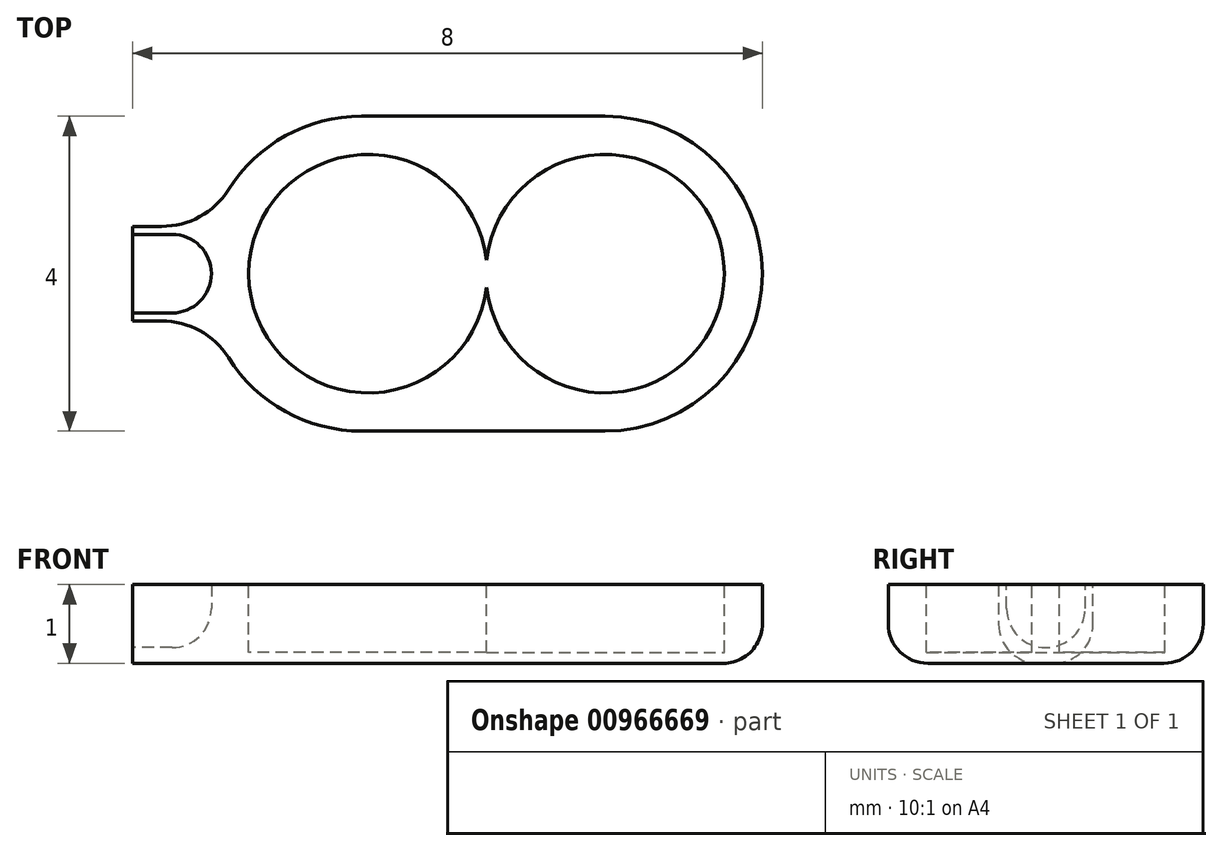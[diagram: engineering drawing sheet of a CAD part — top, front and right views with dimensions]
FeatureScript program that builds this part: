
annotation { "Feature Type Name" : "Feature", "Feature Type Description" : "" }
export const myFeature = defineFeature(function(context is Context, id is Id, definition is map)
    precondition{}
    {
        {
            var Q0;
            Q0=qCreatedBy(makeId("Top.planeOp"),FACE);
            var sketch = newSketch(context, id + "F0", { "sketchPlane" : qUnion([Q0])});
            skLineSegment(sketch, "E0.bottom", {"start": v(0, 0) * mm, "end": v(7, 0) * mm});
            skLineSegment(sketch, "E0.top", {"start": v(0, 4) * mm, "end": v(7, 4) * mm});
            skLineSegment(sketch, "E0.left", {"start": v(0, 0) * mm, "end": v(0, 4) * mm});
            skLineSegment(sketch, "E0.right", {"start": v(7, 0) * mm, "end": v(7, 4) * mm});
            skLineSegment(sketch, "E1", {"start": v(0, 2) * mm, "end": v(0, 2.6) * mm});
            skLineSegment(sketch, "E2", {"start": v(0, 2.6) * mm, "end": v(-1, 2.6) * mm});
            skLineSegment(sketch, "E3", {"start": v(-1, 2.6) * mm, "end": v(-1, 1.4) * mm});
            skLineSegment(sketch, "E4", {"start": v(-1, 1.4) * mm, "end": v(0, 1.4) * mm});
            skSolve(sketch);
        }
        {
            var Q0;
            Q0 = qSketchRegion(id + "F0", true);
            extrude(context, id + "F1", {"entities" : qUnion([Q0]), "depth" : 1 * mm, "offsetDistance" : 25 * mm});
        }
        {
            var Q0;
            Q0=makeQuery(id+"F1.opExtrude","CAP_FACE",FACE,{"disambiguationData":[OSD([sQuery(id+"F0.wireOp",EDGE,"E0.bottom"),sQuery(id+"F0.wireOp",EDGE,"E0.top"),sQuery(id+"F0.wireOp",EDGE,"E0.left"),sQuery(id+"F0.wireOp",EDGE,"E0.right"),sQuery(id+"F0.wireOp",EDGE,"E2"),sQuery(id+"F0.wireOp",EDGE,"E3"),sQuery(id+"F0.wireOp",EDGE,"E4")])],"isStart":false});
            var sketch = newSketch(context, id + "F2", { "sketchPlane" : qUnion([Q0])});
            skLineSegment(sketch, "E5", {"start": v(7, 2) * mm, "end": v(5, 2) * mm});
            skCircle(sketch, "E6", {"center": v(5, 2) * mm, "radius": 1.51 * mm});
            skSolve(sketch);
        }
        {
            var Q0;
            Q0 = qSketchRegion(id + "F2", true);
            extrude(context, id + "F3", {"entities" : qUnion([Q0]), "operationType" : NewBodyOperationType.REMOVE, "oppositeDirection" : true, "depth" : 0.86 * mm, "offsetDistance" : 25 * mm});
        }
        {
            var Q0;
            Q0=makeQuery(id+"F1.opExtrude","CAP_FACE",FACE,{"disambiguationData":[OSD([sQuery(id+"F0.wireOp",EDGE,"E0.bottom"),sQuery(id+"F0.wireOp",EDGE,"E0.top"),sQuery(id+"F0.wireOp",EDGE,"E0.left"),sQuery(id+"F0.wireOp",EDGE,"E0.right"),sQuery(id+"F0.wireOp",EDGE,"E2"),sQuery(id+"F0.wireOp",EDGE,"E3"),sQuery(id+"F0.wireOp",EDGE,"E4")])],"isStart":false});
            var sketch = newSketch(context, id + "F4", { "sketchPlane" : qUnion([Q0])});
            skLineSegment(sketch, "E7", {"start": v(7, 2) * mm, "end": v(2, 2) * mm});
            skCircle(sketch, "E8", {"center": v(2, 2) * mm, "radius": 1.51 * mm});
            skSolve(sketch);
        }
        {
            var Q0;
            Q0 = qSketchRegion(id + "F4", true);
            extrude(context, id + "F5", {"entities" : qUnion([Q0]), "operationType" : NewBodyOperationType.REMOVE, "oppositeDirection" : true, "depth" : 0.86 * mm, "offsetDistance" : 25 * mm});
        }
        {
            var Q0;
            Q0 = qSketchRegion(id + "F4", true);
            extrude(context, id + "F6", {"entities" : qUnion([Q0]), "operationType" : NewBodyOperationType.REMOVE, "oppositeDirection" : true, "depth" : 0.6 * mm, "offsetDistance" : 25 * mm});
        }
        {
            var Q0;
            Q0=makeQuery(id+"F1.opExtrude","CAP_FACE",FACE,{"disambiguationData":[OSD([sQuery(id+"F0.wireOp",EDGE,"E0.bottom"),sQuery(id+"F0.wireOp",EDGE,"E0.top"),sQuery(id+"F0.wireOp",EDGE,"E0.left"),sQuery(id+"F0.wireOp",EDGE,"E0.right"),sQuery(id+"F0.wireOp",EDGE,"E2"),sQuery(id+"F0.wireOp",EDGE,"E3"),sQuery(id+"F0.wireOp",EDGE,"E4")])],"isStart":false});
            var sketch = newSketch(context, id + "F7", { "sketchPlane" : qUnion([Q0])});
            skLineSegment(sketch, "E9", {"start": v(-1, 2) * mm, "end": v(-1, 2.5) * mm});
            skLineSegment(sketch, "E10", {"start": v(-1, 2.5) * mm, "end": v(0, 2.5) * mm});
            skLineSegment(sketch, "E11", {"start": v(0, 2.5) * mm, "end": v(0, 1.5) * mm});
            skLineSegment(sketch, "E12", {"start": v(0, 1.5) * mm, "end": v(-1, 1.5) * mm});
            skLineSegment(sketch, "E13", {"start": v(-1, 1.5) * mm, "end": v(-1, 2) * mm});
            skSolve(sketch);
        }
        {
            var Q0;
            Q0 = qSketchRegion(id + "F7", true);
            extrude(context, id + "F8", {"entities" : qUnion([Q0]), "operationType" : NewBodyOperationType.REMOVE, "oppositeDirection" : true, "depth" : 0.8 * mm, "offsetDistance" : 25 * mm});
        }
        {
            var Q0;
            Q0=makeQuery(id+"F1.opExtrude","SWEPT_EDGE",EDGE,{"disambiguationData":[OSD([sQuery(id+"F0.wireOp",EDGE,"E0.top"),sQuery(id+"F0.wireOp",EDGE,"E0.left")])]});
            var Q1;
            Q1=makeQuery(id+"F1.opExtrude","SWEPT_EDGE",EDGE,{"disambiguationData":[OSD([sQuery(id+"F0.wireOp",EDGE,"E0.top"),sQuery(id+"F0.wireOp",EDGE,"E0.right")])]});
            var Q2;
            Q2=makeQuery(id+"F1.opExtrude","SWEPT_EDGE",EDGE,{"disambiguationData":[OSD([sQuery(id+"F0.wireOp",EDGE,"E0.bottom"),sQuery(id+"F0.wireOp",EDGE,"E0.right")])]});
            var Q3;
            Q3=makeQuery(id+"F1.opExtrude","SWEPT_EDGE",EDGE,{"disambiguationData":[OSD([sQuery(id+"F0.wireOp",EDGE,"E0.bottom"),sQuery(id+"F0.wireOp",EDGE,"E0.left")])]});
            fillet(context, id + "F9", {"entities" : qUnion([Q0, Q1, Q2, Q3]), "radius" : 2 * mm, "tangentPropagation" : true, "allowEdgeOverflow" : false});
        }
        {
            var Q0;
            Q0=makeQuery(id+"F9.opFillet","BLEND_EDGE",EDGE,{"blendedFrom":[makeQuery(id+"F1.opExtrude","SWEPT_EDGE",EDGE,{"disambiguationData":[OSD([sQuery(id+"F0.wireOp",EDGE,"E0.bottom"),sQuery(id+"F0.wireOp",EDGE,"E0.left")])]}),makeQuery(id+"F1.opExtrude","SWEPT_FACE",FACE,{"disambiguationData":[OSD([sQuery(id+"F0.wireOp",EDGE,"E4")])]})],"blendedInto":[makeQuery(id+"F1.opExtrude","SWEPT_FACE",FACE,{"disambiguationData":[OSD([sQuery(id+"F0.wireOp",EDGE,"E4")])]})]});
            var Q1;
            Q1=makeQuery(id+"F9.opFillet","BLEND_EDGE",EDGE,{"blendedFrom":[makeQuery(id+"F1.opExtrude","SWEPT_EDGE",EDGE,{"disambiguationData":[OSD([sQuery(id+"F0.wireOp",EDGE,"E0.top"),sQuery(id+"F0.wireOp",EDGE,"E0.left")])]}),makeQuery(id+"F1.opExtrude","SWEPT_FACE",FACE,{"disambiguationData":[OSD([sQuery(id+"F0.wireOp",EDGE,"E2")])]})],"blendedInto":[makeQuery(id+"F1.opExtrude","SWEPT_FACE",FACE,{"disambiguationData":[OSD([sQuery(id+"F0.wireOp",EDGE,"E2")])]})]});
            fillet(context, id + "F10", {"entities" : qUnion([Q0, Q1]), "radius" : 1 * mm, "tangentPropagation" : true, "allowEdgeOverflow" : false});
        }
        {
            var Q0;
            Q0=makeQuery(id+"F8.boolean.opBoolean","COPY",EDGE,{"derivedFrom":makeQuery(id+"F8.opExtrude","CAP_EDGE",EDGE,{"disambiguationData":[OSD([sQuery(id+"F7.wireOp",EDGE,"E10")])],"isStart":false})});
            var Q1;
            Q1=makeQuery(id+"F8.boolean.opBoolean","COPY",EDGE,{"derivedFrom":makeQuery(id+"F8.opExtrude","CAP_EDGE",EDGE,{"disambiguationData":[OSD([sQuery(id+"F7.wireOp",EDGE,"E12")])],"isStart":false})});
            var Q2;
            Q2=makeQuery(id+"F8.boolean.opBoolean","COPY",EDGE,{"derivedFrom":makeQuery(id+"F8.opExtrude","SWEPT_EDGE",EDGE,{"disambiguationData":[OSD([sQuery(id+"F7.wireOp",EDGE,"E11"),sQuery(id+"F7.wireOp",EDGE,"E12")])]})});
            var Q3;
            Q3=makeQuery(id+"F8.boolean.opBoolean","COPY",EDGE,{"derivedFrom":makeQuery(id+"F8.opExtrude","SWEPT_EDGE",EDGE,{"disambiguationData":[OSD([sQuery(id+"F7.wireOp",EDGE,"E10"),sQuery(id+"F7.wireOp",EDGE,"E11")])]})});
            var Q4;
            Q4=makeQuery(id+"F8.boolean.opBoolean","COPY",EDGE,{"derivedFrom":makeQuery(id+"F8.opExtrude","CAP_EDGE",EDGE,{"disambiguationData":[OSD([sQuery(id+"F7.wireOp",EDGE,"E11")])],"isStart":false})});
            fillet(context, id + "F11", {"entities" : qUnion([Q0, Q1, Q2, Q3, Q4]), "radius" : 0.5 * mm, "tangentPropagation" : true, "allowEdgeOverflow" : false});
        }
        {
            var Q0;
            Q0=makeQuery(id+"F1.opExtrude","CAP_EDGE",EDGE,{"disambiguationData":[OSD([sQuery(id+"F0.wireOp",EDGE,"E0.bottom")])],"isStart":true});
            var Q1;
            {var subQ0=sQuery(id+"F0.wireOp",EDGE,"E0.right");var subQ1=sQuery(id+"F0.wireOp",EDGE,"E0.bottom");Q1=makeQuery(id+"F9.opFillet","BLEND_EDGE",EDGE,{"blendedFrom":[makeQuery(id+"F1.opExtrude","SWEPT_EDGE",EDGE,{"disambiguationData":[OSD([subQ1,subQ0])]}),makeQuery(id+"F1.opExtrude","CAP_FACE",FACE,{"disambiguationData":[OSD([subQ1,sQuery(id+"F0.wireOp",EDGE,"E0.top"),sQuery(id+"F0.wireOp",EDGE,"E0.left"),subQ0,sQuery(id+"F0.wireOp",EDGE,"E2"),sQuery(id+"F0.wireOp",EDGE,"E3"),sQuery(id+"F0.wireOp",EDGE,"E4")])],"isStart":true})],"blendedInto":[makeQuery(id+"F1.opExtrude","CAP_FACE",FACE,{"disambiguationData":[OSD([subQ1,sQuery(id+"F0.wireOp",EDGE,"E0.top"),sQuery(id+"F0.wireOp",EDGE,"E0.left"),subQ0,sQuery(id+"F0.wireOp",EDGE,"E2"),sQuery(id+"F0.wireOp",EDGE,"E3"),sQuery(id+"F0.wireOp",EDGE,"E4")])],"isStart":true})]});}
            fillet(context, id + "F12", {"entities" : qUnion([Q0, Q1]), "radius" : 0.5 * mm, "tangentPropagation" : true, "allowEdgeOverflow" : false});
        }
    });
